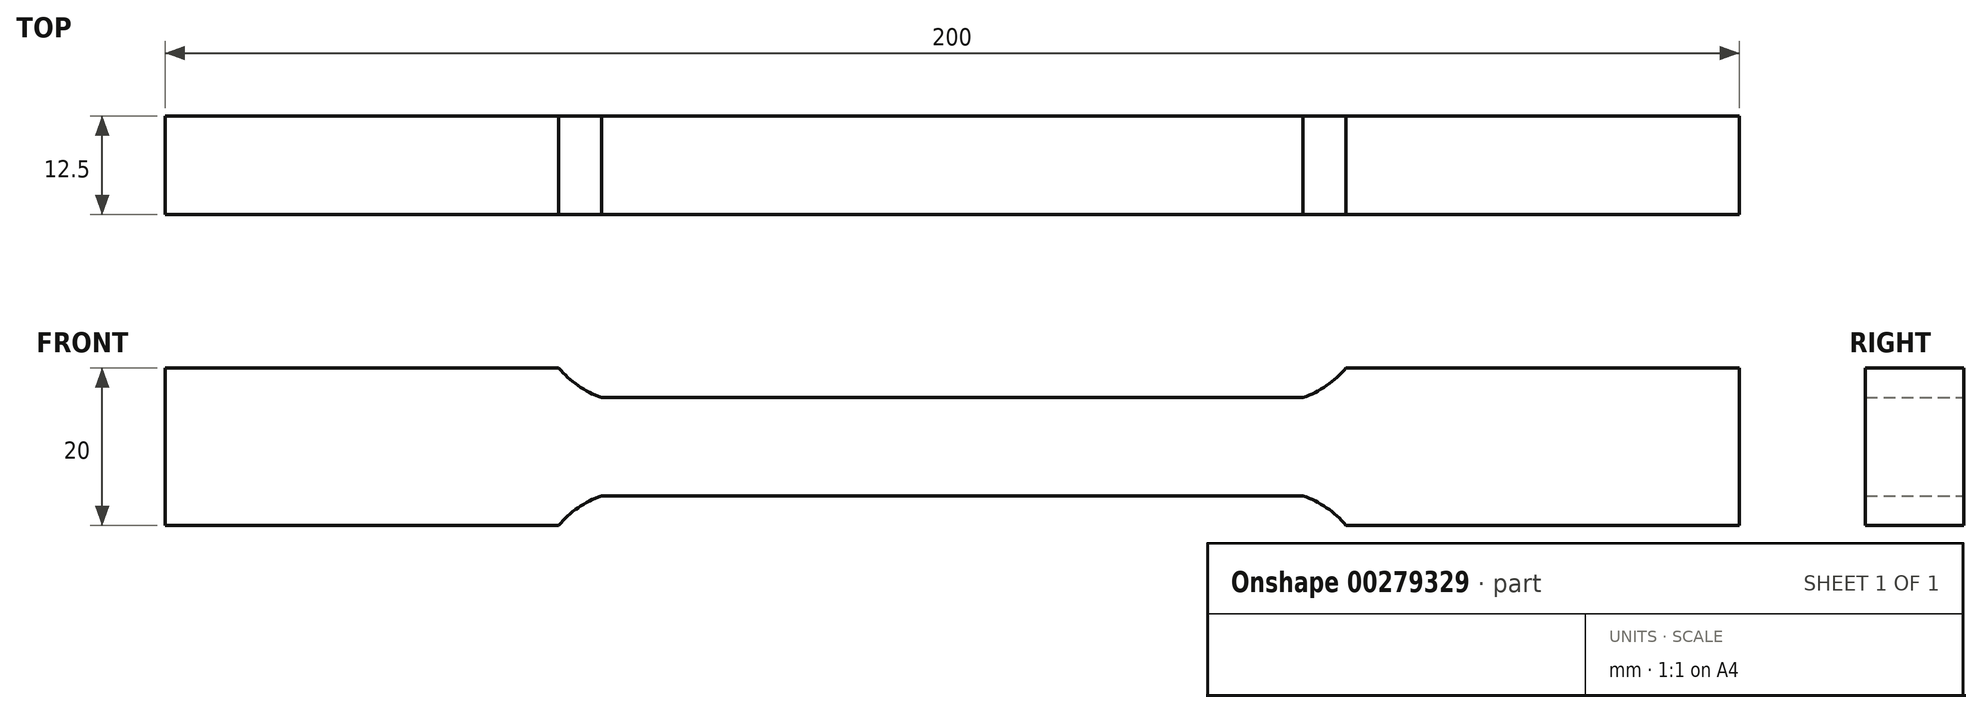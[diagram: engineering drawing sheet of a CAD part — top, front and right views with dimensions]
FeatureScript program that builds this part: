
annotation { "Feature Type Name" : "Feature", "Feature Type Description" : "" }
export const myFeature = defineFeature(function(context is Context, id is Id, definition is map)
    precondition{}
    {
        {
            var Q0;
            Q0=qCreatedBy(makeId("Front.planeOp"),FACE);
            var sketch = newSketch(context, id + "F0", { "sketchPlane" : qUnion([Q0])});
            skLineSegment(sketch, "E0", {"start": v(0, 6.25) * mm, "end": v(44.57, 6.25) * mm});
            skArc(sketch, "E1", {"start": v(44.57, 6.25) * mm, "mid": v(47.54, 7.76) * mm, "end": v(50, 10) * mm});
            skLineSegment(sketch, "E2", {"start": v(50, 10) * mm, "end": v(100, 10) * mm});
            skLineSegment(sketch, "E3", {"start": v(100, 10) * mm, "end": v(100, 0) * mm});
            skLineSegment(sketch, "E4.MirrorCS", {"start": v(0, -6.25) * mm, "end": v(44.57, -6.25) * mm});
            skLineSegment(sketch, "E5.MirrorCS", {"start": v(100, -10) * mm, "end": v(100, 0) * mm});
            skLineSegment(sketch, "E6.MirrorCS", {"start": v(50, -10) * mm, "end": v(100, -10) * mm});
            skArc(sketch, "E7.MirrorCS", {"start": v(44.57, -6.25) * mm, "mid": v(47.54, -7.76) * mm, "end": v(50, -10) * mm});
            skArc(sketch, "E8.MirrorCS", {"start": v(-44.57, -6.25) * mm, "mid": v(-47.54, -7.76) * mm, "end": v(-50, -10) * mm});
            skLineSegment(sketch, "E9.MirrorCS", {"start": v(-50, -10) * mm, "end": v(-100, -10) * mm});
            skLineSegment(sketch, "E10.MirrorCS", {"start": v(0, 6.25) * mm, "end": v(-44.57, 6.25) * mm});
            skArc(sketch, "E11.MirrorCS", {"start": v(-44.57, 6.25) * mm, "mid": v(-47.54, 7.76) * mm, "end": v(-50, 10) * mm});
            skLineSegment(sketch, "E12.MirrorCS", {"start": v(-50, 10) * mm, "end": v(-100, 10) * mm});
            skLineSegment(sketch, "E13.MirrorCS", {"start": v(-100, -10) * mm, "end": v(-100, 0) * mm});
            skLineSegment(sketch, "E14.MirrorCS", {"start": v(-100, 10) * mm, "end": v(-100, 0) * mm});
            skLineSegment(sketch, "E15.MirrorCS", {"start": v(0, -6.25) * mm, "end": v(-44.57, -6.25) * mm});
            skSolve(sketch);
        }
        {
            var Q0;
            Q0 = qSketchRegion(id + "F0", true);
            extrude(context, id + "F1", {"entities" : qUnion([Q0]), "endBound" : BoundingType.SYMMETRIC, "depth" : 12.5 * mm});
        }
    });
